# Revit family: Sanitary_Installation-Systems_hansgrohe_15743001-ShowerSelect-S-Thermostat-for-c_
name_source: partatom
category: Plumbing Fixtures
revit_build: Autodesk Revit 2015 (Build: 20140903_1530(x64)
units: mm (PartAtom-declared; Revit-internal decimal feet)

## types (1)
- Chrome 000
    BIMobject category = Installation Systems
    BIMobject category code = sanitary-installation-systems
    BIMobject main category = Sanitary
    BIMobject main category code = sanitary
    BOSUseNativeGeometries = 1
    Brand url = http://www.hansgrohe-int.com
    Default Elevation = 4' - 0"
    EAN code = https://4011097740379
    Edition number = 1
    IFC Classification = Sanitary Terminal
    Installation instructions = https://pro.hansgrohe-usa.com
    Manufacturer country = Germany
    Manufacturer name = hansgrohe
    Masterformat 2014 Code = 40 05 89
    Masterformat 2014 Description = Valve Accessories
    Material main = Chrome
    NBS Reference Code = 31-75
    NBS Reference Description = Sanitary Accessories
    OmniClass Code = 23-27 31 29 15
    OmniClass Description = Thermostatically Controlled Mixing Valves
    Product Guid = 44bf0ed5-0d9a-43f9-88f4-646a4887ea65
    Product SKU = 15743001
    Product data url = https://bimobject.com
    Product family = ShowerSelect S
    Product group = Shower thermostat
    Product name = 15743001 ShowerSelect S Thermostat for concealed installation for 2 function 15743001
    Product url = https://pro.hansgrohe-usa.com
    QR code = http://bimobject.com
    Technical description = https://pro.hansgrohe-usa.com
    UNSPSC Code = 301815
    Uniclass 1.4 Code = L721
    Uniclass 1.4 Description = Sanitary equipment
    Uniclass 2.0 Code = PR-31-75
    Uniclass 2.0 Description = Sanitary Accessories
    Uniclass 2015 Code = Pr_40_20_76
    Uniclass 2015 Name = Sanitary accessories
    Uniformat II Code = D20
    Uniformat II Description = PLUMBING

## geometry (parser evidence)
native form markers: Sweep x3
no freeform markers — native parametric forms only
